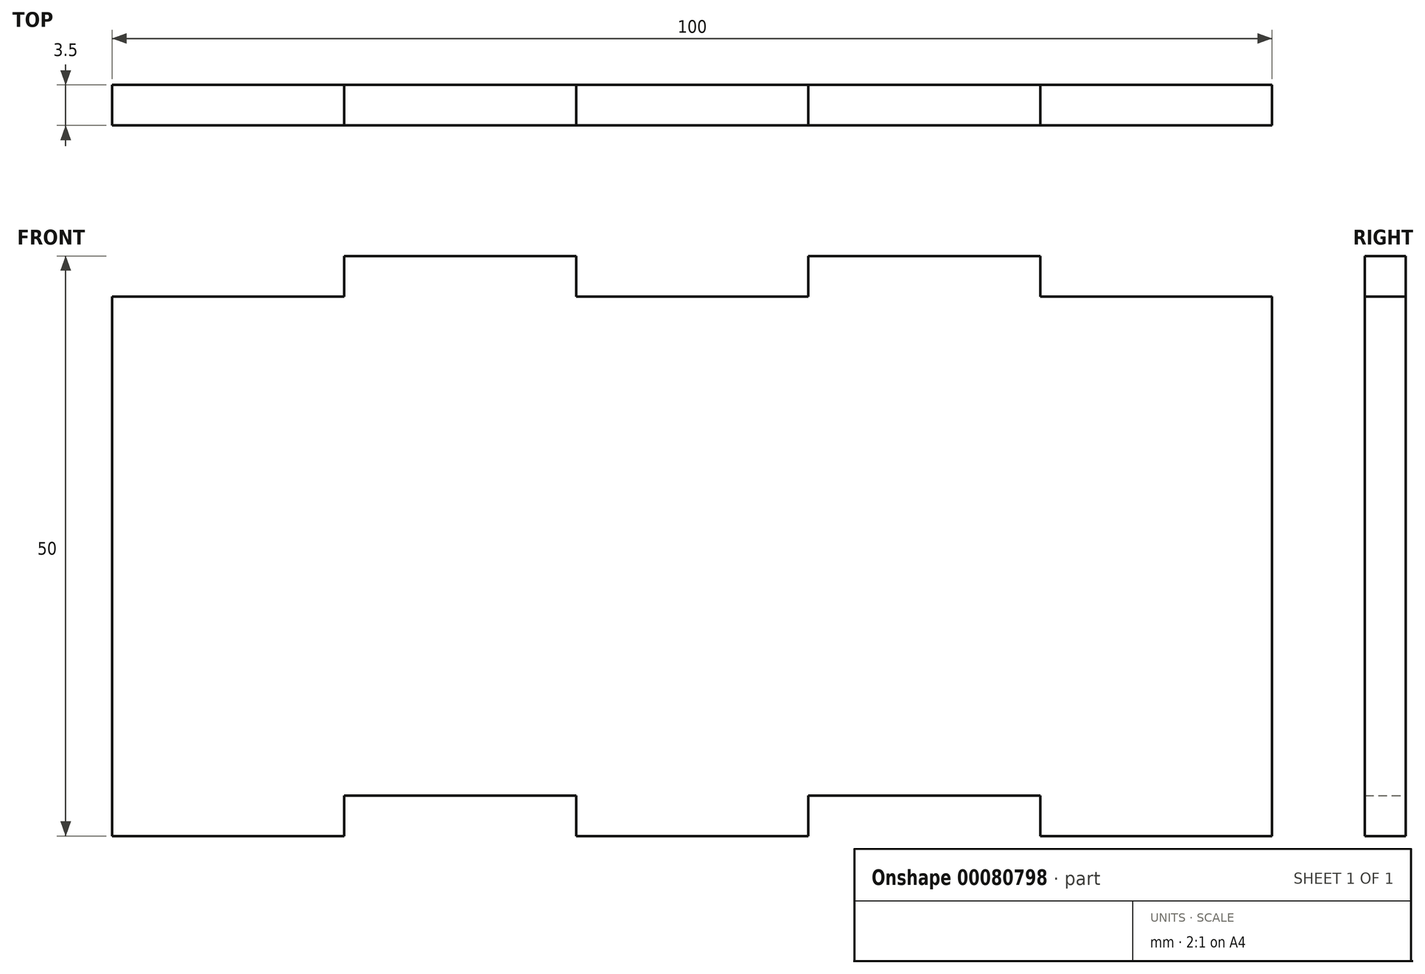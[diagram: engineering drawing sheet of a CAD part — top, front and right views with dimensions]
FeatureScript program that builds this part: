
annotation { "Feature Type Name" : "Feature", "Feature Type Description" : "" }
export const myFeature = defineFeature(function(context is Context, id is Id, definition is map)
    precondition{}
    {
        {
            var Q0;
            Q0=qCreatedBy(makeId("Front.planeOp"),FACE);
            var sketch = newSketch(context, id + "F0", { "sketchPlane" : qUnion([Q0])});
            skLineSegment(sketch, "E0.bottom", {"start": v(-60, -48.08) * mm, "end": v(40, -48.08) * mm});
            skLineSegment(sketch, "E0.top", {"start": v(-60, -98.08) * mm, "end": v(40, -98.08) * mm});
            skLineSegment(sketch, "E0.left", {"start": v(-60, -48.08) * mm, "end": v(-60, -98.08) * mm});
            skLineSegment(sketch, "E0.right", {"start": v(40, -48.08) * mm, "end": v(40, -98.08) * mm});
            skLineSegment(sketch, "E1.direction1", {"start": v(-60, -98.08) * mm, "end": v(-49.65, -98.08) * mm, "construction": true});
            skLineSegment(sketch, "E2", {"start": v(-40, -98.08) * mm, "end": v(-40, -94.58) * mm});
            skLineSegment(sketch, "E3", {"start": v(-40, -94.58) * mm, "end": v(-20, -94.58) * mm});
            skLineSegment(sketch, "E4", {"start": v(-20, -94.58) * mm, "end": v(-20, -98.08) * mm});
            skLineSegment(sketch, "E5", {"start": v(-20, -98.08) * mm, "end": v(0, -98.08) * mm});
            skLineSegment(sketch, "E6", {"start": v(0, -98.08) * mm, "end": v(0, -94.58) * mm});
            skLineSegment(sketch, "E7", {"start": v(-60, -98.08) * mm, "end": v(-40, -98.08) * mm});
            skLineSegment(sketch, "E8", {"start": v(0, -94.58) * mm, "end": v(20, -94.58) * mm});
            skLineSegment(sketch, "E9", {"start": v(20, -94.58) * mm, "end": v(20, -98.08) * mm});
            skLineSegment(sketch, "E10", {"start": v(-60, -51.58) * mm, "end": v(-40, -51.58) * mm});
            skLineSegment(sketch, "E11", {"start": v(-40, -51.58) * mm, "end": v(-40, -48.08) * mm});
            skLineSegment(sketch, "E12", {"start": v(-40, -48.08) * mm, "end": v(-20, -48.08) * mm});
            skLineSegment(sketch, "E13", {"start": v(-20, -48.08) * mm, "end": v(-20, -51.58) * mm});
            skLineSegment(sketch, "E14", {"start": v(-20, -51.58) * mm, "end": v(0, -51.58) * mm});
            skLineSegment(sketch, "E15", {"start": v(0, -51.58) * mm, "end": v(0, -48.08) * mm});
            skLineSegment(sketch, "E16", {"start": v(0, -48.08) * mm, "end": v(20, -48.08) * mm});
            skLineSegment(sketch, "E17", {"start": v(20, -48.08) * mm, "end": v(20, -51.58) * mm});
            skLineSegment(sketch, "E18", {"start": v(20, -51.58) * mm, "end": v(40, -51.58) * mm});
            skSolve(sketch);
        }
        {
            var Q0;
            Q0=makeQuery(id+"F0.imprint","IMPRINT",FACE,{"disambiguationData":[TD([[makeQuery(id+"F0.imprint","IMPRINT",EDGE,{"derivedFrom":sQuery(id+"F0.wireOp",EDGE,"E2")}),1.0]])]});
            extrude(context, id + "F1", {"entities" : qUnion([Q0]), "depth" : 3.5 * mm});
        }
    });
